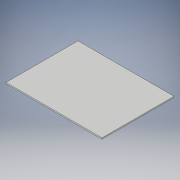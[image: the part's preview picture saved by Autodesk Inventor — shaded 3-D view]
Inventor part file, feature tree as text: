
AUTODESK INVENTOR PART (.ipt)
format: ipt  version: 2019 (Build 230136000, 136)  size: 89,600 bytes
history: native  units: mm
features: extrude x1, sketch x1
ambient origin geometry x8: Origin, YZ Plane, XZ Plane, XY Plane, X Axis, Y Axis, Z Axis, Center Point
bodies: Body1 (feature_tree)
feature tree (2):
  extrude  "Extrusion2"  Depth=300.0mm
  sketch  "Sketch1"  dims[d0=400.0mm d1=300.0mm d4=5.0mm d5=0.0mm]
